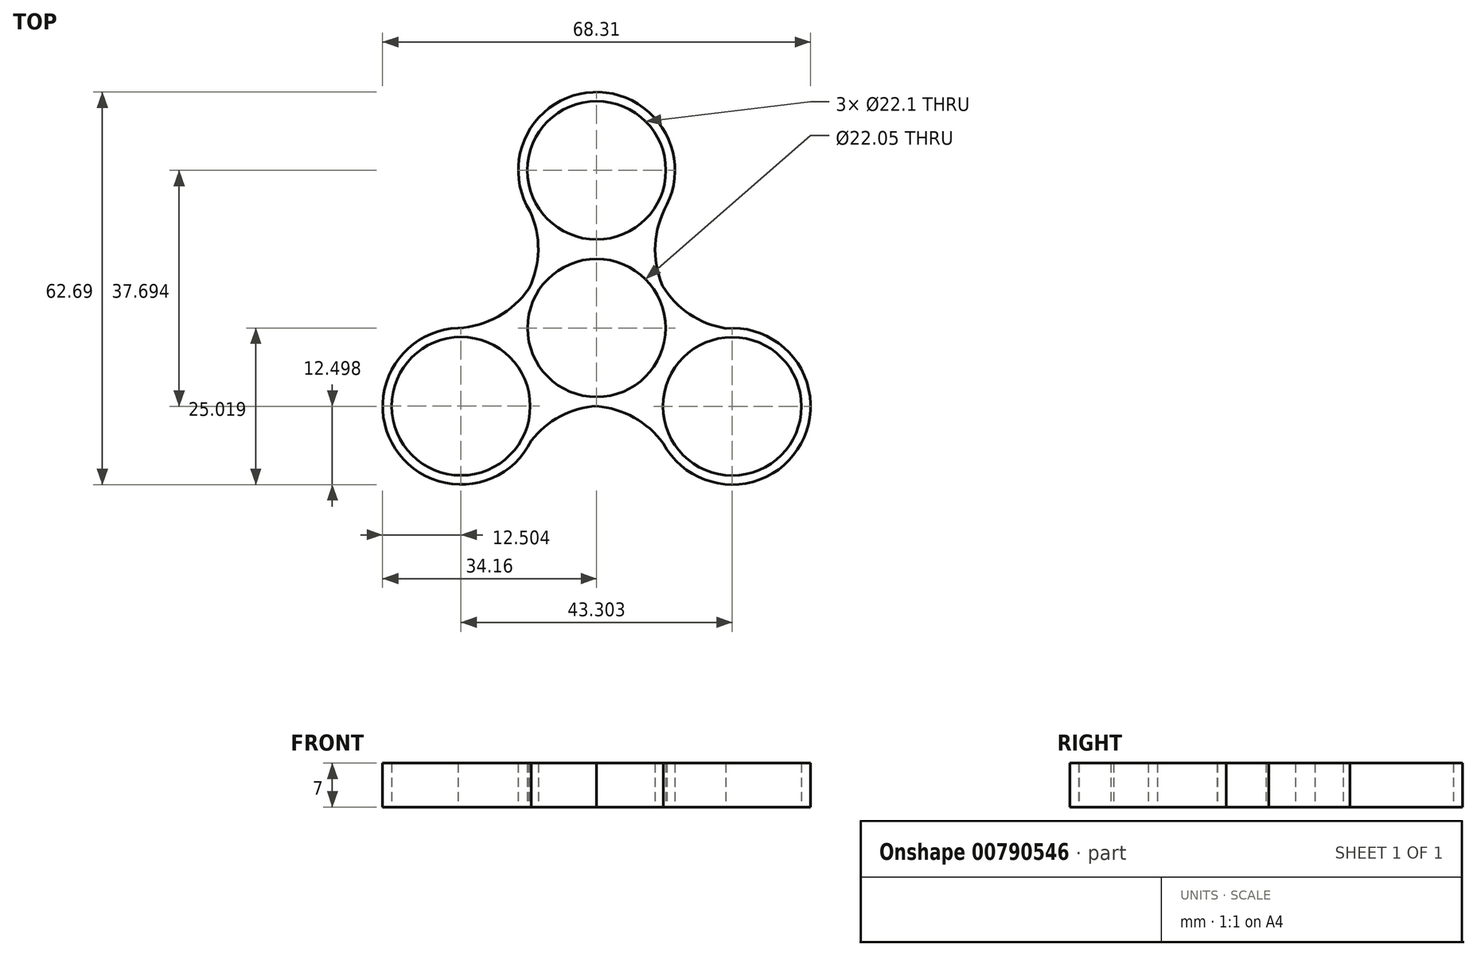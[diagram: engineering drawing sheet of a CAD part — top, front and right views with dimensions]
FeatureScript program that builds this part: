
annotation { "Feature Type Name" : "Feature", "Feature Type Description" : "" }
export const myFeature = defineFeature(function(context is Context, id is Id, definition is map)
    precondition{}
    {
        {
            var Q0;
            Q0=qCreatedBy(makeId("Top.planeOp"),FACE);
            var sketch = newSketch(context, id + "F0", { "sketchPlane" : qUnion([Q0])});
            skCircle(sketch, "E0", {"center": v(-1.9, 8.79) * mm, "radius": 11.03 * mm});
            skCircle(sketch, "E1", {"center": v(-1.9, 8.79) * mm, "radius": 12.5 * mm});
            skCircle(sketch, "E2", {"center": v(-1.9, 33.96) * mm, "radius": 11.05 * mm});
            skCircle(sketch, "E3", {"center": v(-1.9, 33.96) * mm, "radius": 12.5 * mm});
            skCircle(sketch, "E4", {"center": v(19.76, -3.73) * mm, "radius": 11.05 * mm});
            skCircle(sketch, "E5", {"center": v(19.76, -3.73) * mm, "radius": 12.5 * mm});
            skCircle(sketch, "E6", {"center": v(-23.55, -3.71) * mm, "radius": 11.05 * mm});
            skCircle(sketch, "E7", {"center": v(-23.55, -3.71) * mm, "radius": 12.5 * mm});
            skArc(sketch, "E8", {"start": v(8.76, -9.67) * mm, "mid": v(4.09, -5.52) * mm, "end": v(-1.9, -3.71) * mm});
            skArc(sketch, "E9", {"start": v(-1.9, -3.71) * mm, "mid": v(-7.71, -5.34) * mm, "end": v(-12.33, -9.23) * mm});
            skArc(sketch, "E10", {"start": v(-24, 8.78) * mm, "mid": v(-17.61, 10.6) * mm, "end": v(-12.7, 15.07) * mm});
            skArc(sketch, "E11", {"start": v(-12.7, 15.07) * mm, "mid": v(-11.2, 21.23) * mm, "end": v(-12.54, 27.42) * mm});
            skArc(sketch, "E12", {"start": v(9.35, 28.5) * mm, "mid": v(7.47, 22.09) * mm, "end": v(8.64, 15.52) * mm});
            skArc(sketch, "E13", {"start": v(8.64, 15.52) * mm, "mid": v(12.92, 11) * mm, "end": v(18.72, 8.73) * mm});
            skSolve(sketch);
        }
        {
            var Q0;
            Q0=makeQuery(id+"F0.imprint","IMPRINT",FACE,{"disambiguationData":[TD([[makeQuery(id+"F0.imprint","IMPRINT",EDGE,{"derivedFrom":sQuery(id+"F0.wireOp",EDGE,"E6")}),-1.0]])]});
            var Q1;
            Q1=makeQuery(id+"F0.imprint","IMPRINT",FACE,{"disambiguationData":[TD([[makeQuery(id+"F0.imprint","IMPRINT",EDGE,{"derivedFrom":sQuery(id+"F0.wireOp",EDGE,"E0")}),-1.0]])]});
            var Q2;
            {var subQ0=sQuery(id+"F0.wireOp",EDGE,"E9");Q2=makeQuery(id+"F0.imprint","IMPRINT",FACE,{"disambiguationData":[TD([[makeQuery(id+"F0.imprint","IMPRINT",EDGE,{"derivedFrom":subQ0}),-1.0]])]});}
            var Q3;
            {var subQ0=sQuery(id+"F0.wireOp",EDGE,"E10");Q3=makeQuery(id+"F0.imprint","IMPRINT",FACE,{"disambiguationData":[TD([[makeQuery(id+"F0.imprint","IMPRINT",EDGE,{"derivedFrom":subQ0}),-1.0]])]});}
            var Q4;
            {var subQ0=sQuery(id+"F0.wireOp",EDGE,"E8");Q4=makeQuery(id+"F0.imprint","IMPRINT",FACE,{"disambiguationData":[TD([[makeQuery(id+"F0.imprint","IMPRINT",EDGE,{"derivedFrom":subQ0}),-1.0]])]});}
            var Q5;
            Q5=makeQuery(id+"F0.imprint","IMPRINT",FACE,{"disambiguationData":[TD([[makeQuery(id+"F0.imprint","IMPRINT",EDGE,{"derivedFrom":sQuery(id+"F0.wireOp",EDGE,"E4")}),-1.0]])]});
            var Q6;
            {var subQ0=sQuery(id+"F0.wireOp",EDGE,"E11");Q6=makeQuery(id+"F0.imprint","IMPRINT",FACE,{"disambiguationData":[TD([[makeQuery(id+"F0.imprint","IMPRINT",EDGE,{"derivedFrom":subQ0}),-1.0]])]});}
            var Q7;
            {var subQ0=sQuery(id+"F0.wireOp",EDGE,"E13");Q7=makeQuery(id+"F0.imprint","IMPRINT",FACE,{"disambiguationData":[TD([[makeQuery(id+"F0.imprint","IMPRINT",EDGE,{"derivedFrom":subQ0}),-1.0]])]});}
            var Q8;
            Q8=makeQuery(id+"F0.imprint","IMPRINT",FACE,{"disambiguationData":[TD([[makeQuery(id+"F0.imprint","IMPRINT",EDGE,{"derivedFrom":sQuery(id+"F0.wireOp",EDGE,"E2")}),-1.0]])]});
            extrude(context, id + "F1", {"entities" : qUnion([Q0, Q1, Q2, Q3, Q4, Q5, Q6, Q7, Q8]), "depth" : 7 * mm, "offsetDistance" : 25 * mm});
        }
    });
